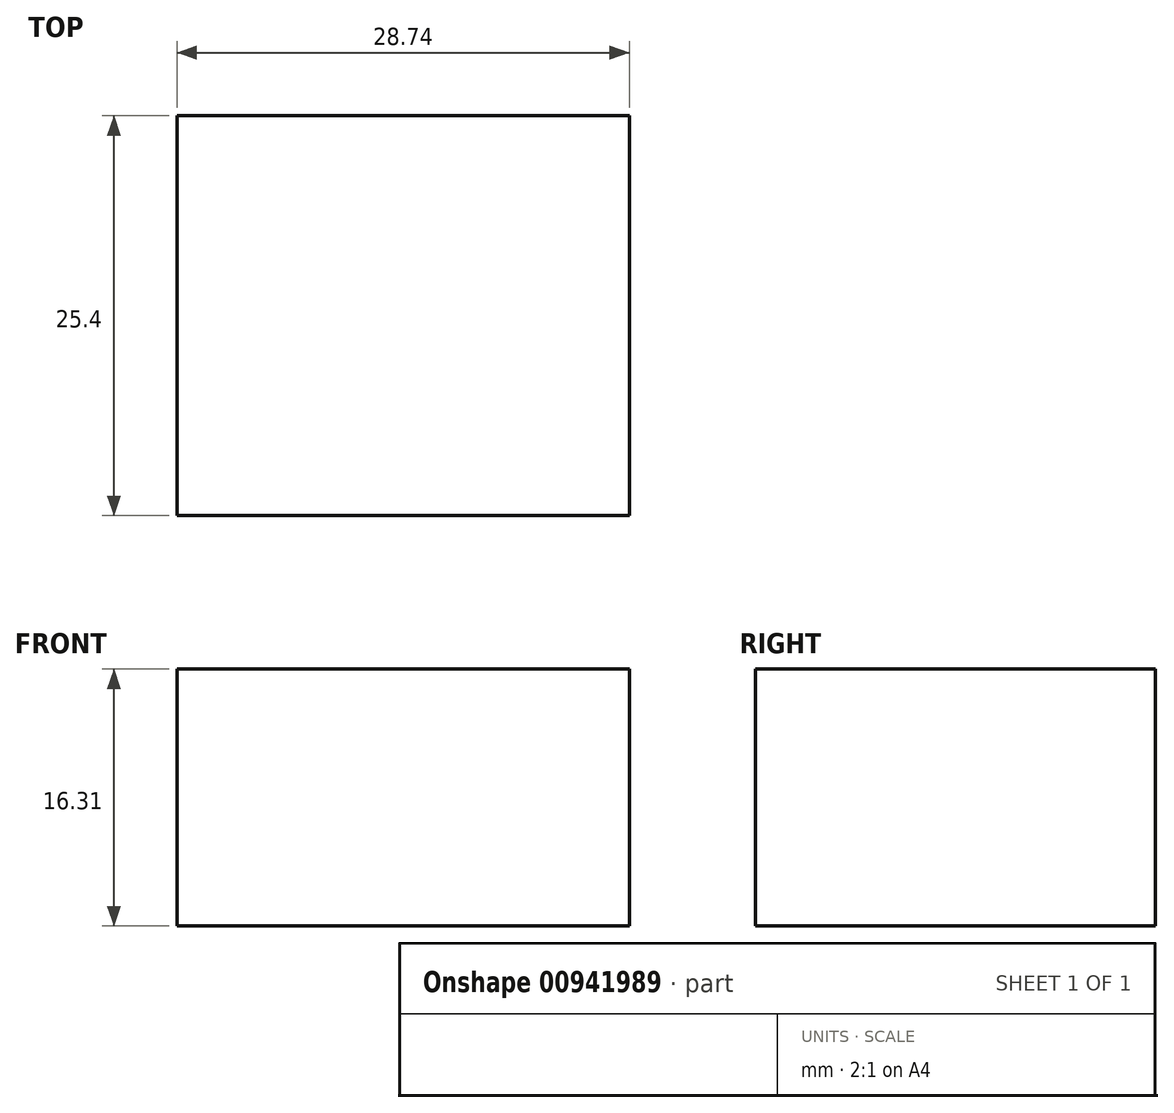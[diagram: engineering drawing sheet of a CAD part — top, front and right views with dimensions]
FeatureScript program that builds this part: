
annotation { "Feature Type Name" : "Feature", "Feature Type Description" : "" }
export const myFeature = defineFeature(function(context is Context, id is Id, definition is map)
    precondition{}
    {
        {
            var Q0;
            Q0=qCreatedBy(makeId("Front.planeOp"),FACE);
            var sketch = newSketch(context, id + "F0", { "sketchPlane" : qUnion([Q0])});
            skLineSegment(sketch, "E0.bottom", {"start": v(68.9, 20.03) * mm, "end": v(97.65, 20.03) * mm});
            skLineSegment(sketch, "E0.top", {"start": v(68.9, 3.72) * mm, "end": v(97.65, 3.72) * mm});
            skLineSegment(sketch, "E0.left", {"start": v(68.9, 20.03) * mm, "end": v(68.9, 3.72) * mm});
            skLineSegment(sketch, "E0.right", {"start": v(97.65, 20.03) * mm, "end": v(97.65, 3.72) * mm});
            skSolve(sketch);
        }
        {
            var Q0;
            Q0 = qSketchRegion(id + "F0", true);
            extrude(context, id + "F1", {"entities" : qUnion([Q0]), "depth" : 25.4 * mm, "offsetDistance" : 25.4 * mm});
        }
    });
